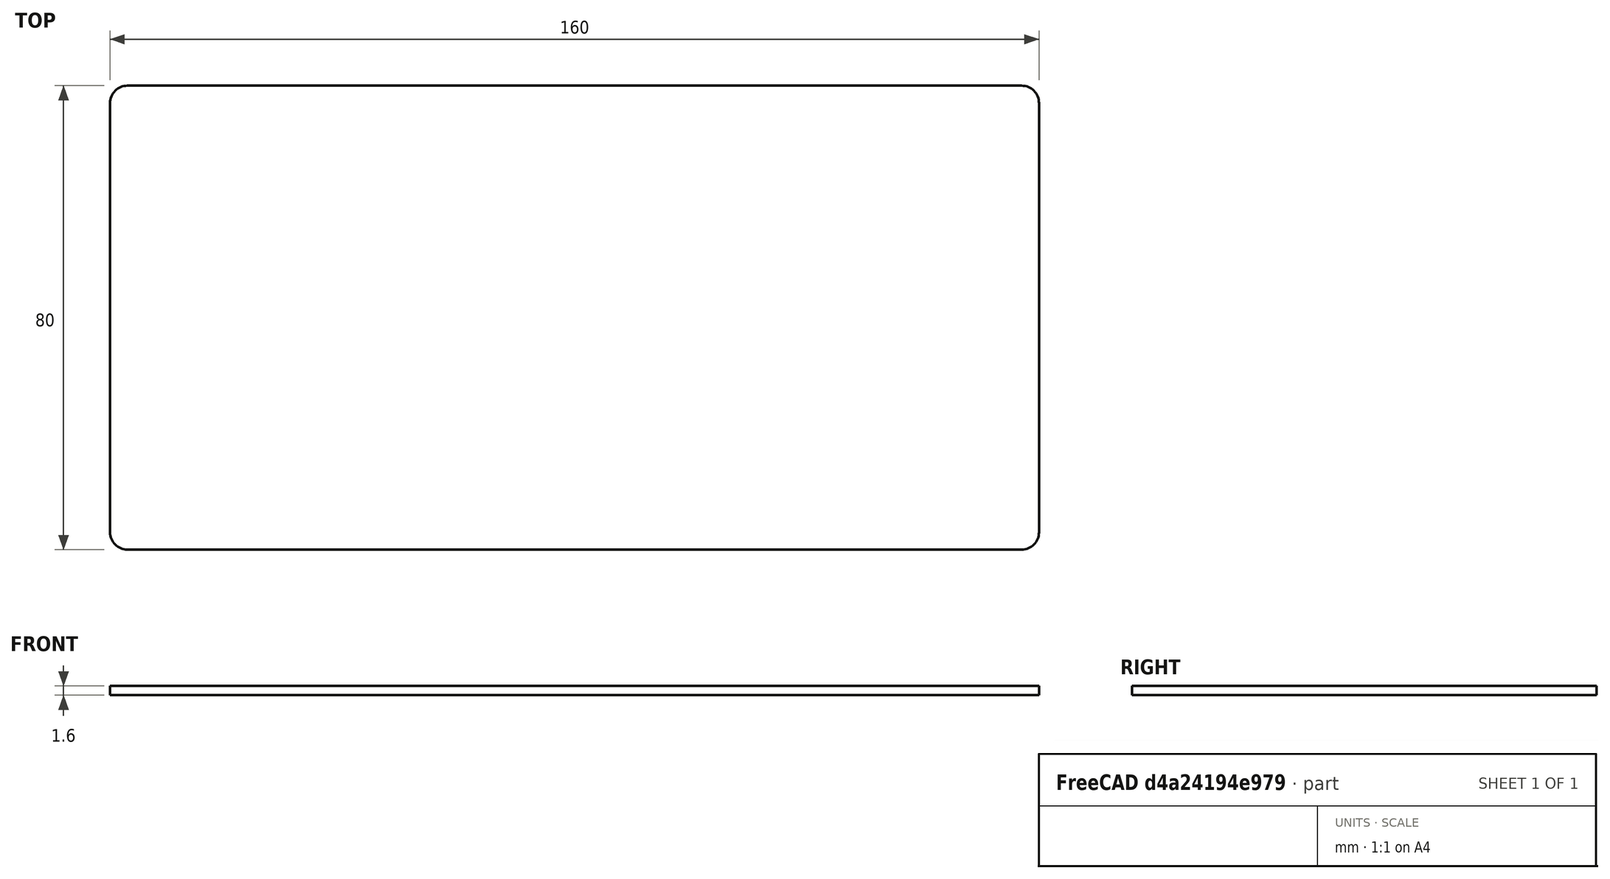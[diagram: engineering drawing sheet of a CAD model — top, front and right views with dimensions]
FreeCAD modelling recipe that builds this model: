
FCSTD DOCUMENT  (FreeCAD 0.20R29177 +426 (Git))
Label: box
License: All rights reserved
LicenseURL: http://en.wikipedia.org/wiki/All_rights_reserved
objects: Sketcher::SketchObject×1, PartDesign::Pad×1, PartDesign::Body×1, App::Part×1
note: 4 computed .brp shape members not serialized (recipe doc carries the construction recipe); baked Part::Feature solids carry a one-line shape summary decoded from their .brp

FEATURE [Sketcher::SketchObject] Sketch  label="PCB001"
  FullyConstrained = true
  MapMode = 5
  Support = -> [XY_Plane001]
  sketch-geometry (8):
    g0: LineSegment StartX=-77 StartY=40 StartZ=0 EndX=77 EndY=40 EndZ=0
    g1: LineSegment StartX=80 StartY=37 StartZ=0 EndX=80 EndY=-37 EndZ=0
    g2: LineSegment StartX=77 StartY=-40 StartZ=0 EndX=-77 EndY=-40 EndZ=0
    g3: LineSegment StartX=-80 StartY=-37 StartZ=0 EndX=-80 EndY=37 EndZ=0
    g4: ArcOfCircle CenterX=-77 CenterY=37 CenterZ=0 NormalX=0 NormalY=0 NormalZ=1 AngleXU=0 Radius=3 StartAngle=1.5708 EndAngle=3.14159
    g5: ArcOfCircle CenterX=-77 CenterY=-37 CenterZ=0 NormalX=0 NormalY=0 NormalZ=1 AngleXU=0 Radius=3 StartAngle=3.14159 EndAngle=4.71239
    g6: ArcOfCircle CenterX=77 CenterY=-37 CenterZ=0 NormalX=0 NormalY=0 NormalZ=1 AngleXU=0 Radius=3 StartAngle=4.71239 EndAngle=6.28319
    g7: ArcOfCircle CenterX=77 CenterY=37 CenterZ=0 NormalX=0 NormalY=0 NormalZ=1 AngleXU=0 Radius=3 StartAngle=3.4079e-12 EndAngle=1.5708
  constraints (18):
    c: Horizontal(g0)
    c: Horizontal(g2)
    c: Vertical(g1)
    c: Vertical(g3)
    c: Tangent(g0,g4) = 1.5708
    c: Tangent(g3,g4) = 1.5708
    c: Tangent(g3,g5) = 1.5708
    c: Tangent(g2,g5) = 1.5708
    c: Tangent(g2,g6) = 1.5708
    c: Tangent(g1,g6) = 1.5708
    c: Tangent(g1,g7) = 1.5708
    c: Tangent(g0,g7) = 1.5708
    c: DistanceY(g2,g0) = 80
    c: DistanceX(g3,g1) = 160
    c: Symmetric(g3,g1,g-2)
    c: Symmetric(g0,g2,g-1)
    c: Equal(g7,g6)
    c: Radius(g4) = 3
FEATURE [PartDesign::Pad] Pad
  Direction = (0,0,1)
  Length = 1.6
  Length2 = 10
  Profile = -> Sketch
  ReferenceAxis = -> Sketch [N_Axis]
  Type = 0
FEATURE [PartDesign::Body] Body  label="PCB"
  Group = -> [Sketch,Pad]
  Origin = -> Origin001
  Tip = -> Pad
FEATURE [App::Part] Part  label="Debud_box"
  Group = -> [Body]
  Origin = -> Origin
